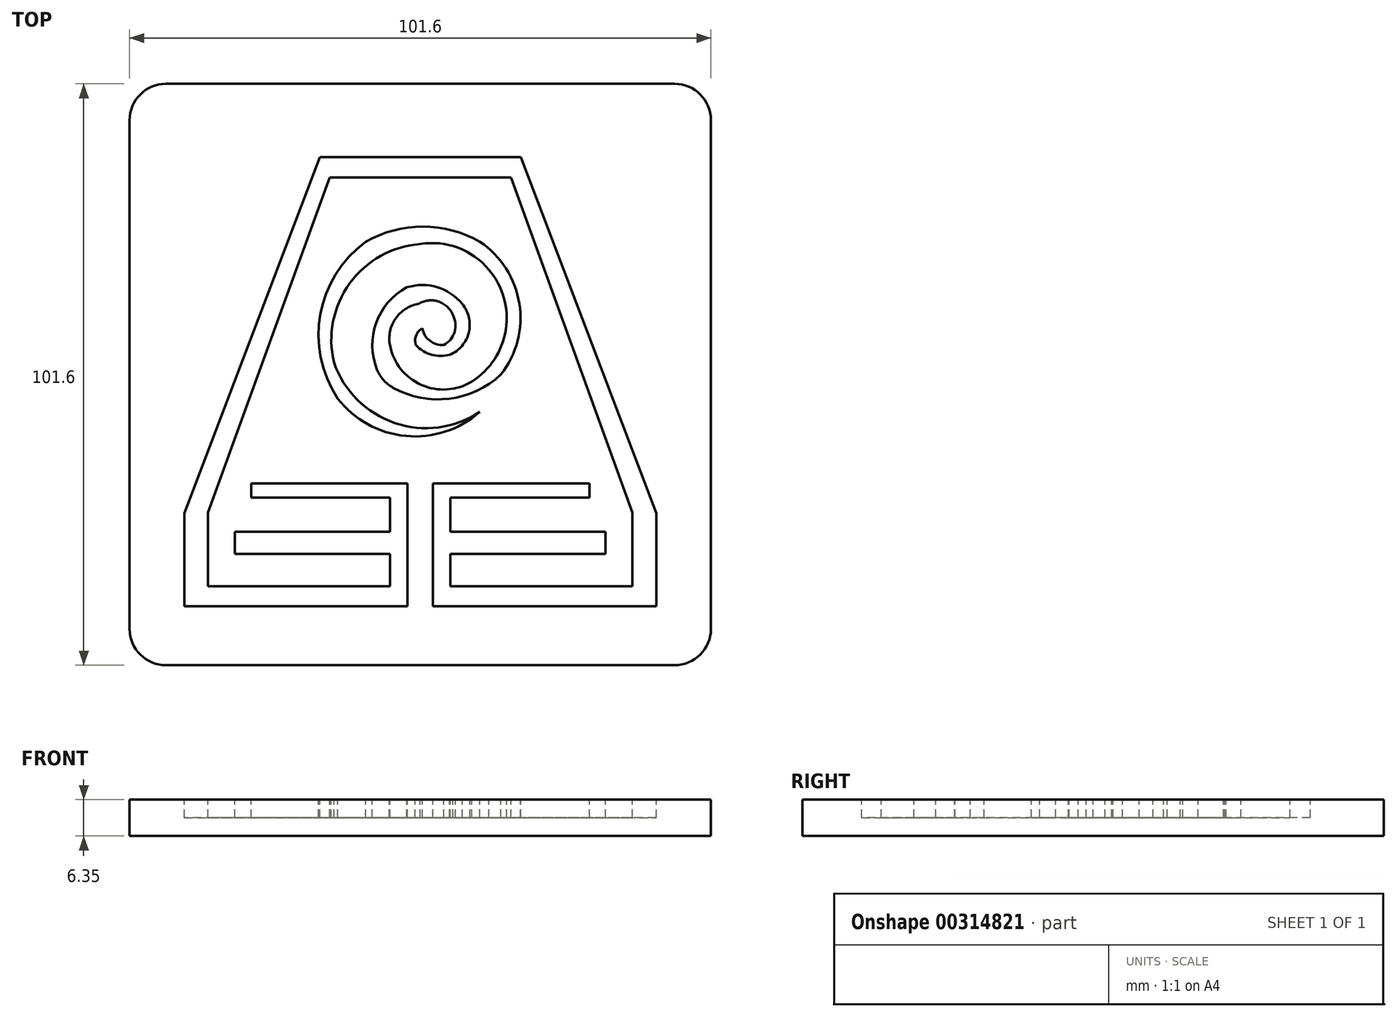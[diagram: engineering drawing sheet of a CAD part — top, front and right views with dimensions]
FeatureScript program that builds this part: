
annotation { "Feature Type Name" : "Feature", "Feature Type Description" : "" }
export const myFeature = defineFeature(function(context is Context, id is Id, definition is map)
    precondition{}
    {
        {
            var Q0;
            Q0=qCreatedBy(makeId("Top.planeOp"),FACE);
            var sketch = newSketch(context, id + "F0", { "sketchPlane" : qUnion([Q0])});
            skLineSegment(sketch, "E0.bottom", {"start": v(-44.45, 50.8) * mm, "end": v(44.45, 50.8) * mm});
            skLineSegment(sketch, "E0.top", {"start": v(-44.45, -50.8) * mm, "end": v(44.45, -50.8) * mm});
            skLineSegment(sketch, "E0.left", {"start": v(-50.8, 44.45) * mm, "end": v(-50.8, -44.45) * mm});
            skLineSegment(sketch, "E0.right", {"start": v(50.8, 44.45) * mm, "end": v(50.8, -44.45) * mm});
            skPoint(sketch, "E1.visualSharp", {"position": v(-50.8, 50.8) * mm});
            skArc(sketch, "E1.filletArc", {"start": v(-44.45, 50.8) * mm, "mid": v(-48.94, 48.94) * mm, "end": v(-50.8, 44.45) * mm});
            skPoint(sketch, "E2.visualSharp", {"position": v(50.8, 50.8) * mm});
            skArc(sketch, "E2.filletArc", {"start": v(50.8, 44.45) * mm, "mid": v(48.94, 48.94) * mm, "end": v(44.45, 50.8) * mm});
            skPoint(sketch, "E3.visualSharp", {"position": v(50.8, -50.8) * mm});
            skArc(sketch, "E3.filletArc", {"start": v(44.45, -50.8) * mm, "mid": v(48.94, -48.94) * mm, "end": v(50.8, -44.45) * mm});
            skPoint(sketch, "E4.visualSharp", {"position": v(-50.8, -50.8) * mm});
            skArc(sketch, "E4.filletArc", {"start": v(-50.8, -44.45) * mm, "mid": v(-48.94, -48.94) * mm, "end": v(-44.45, -50.8) * mm});
            skSolve(sketch);
        }
        {
            var Q0;
            Q0 = qSketchRegion(id + "F0", true);
            extrude(context, id + "F1", {"entities" : qUnion([Q0]), "depth" : 6.35 * mm});
        }
        {
            var Q0;
            Q0=makeQuery(id+"F1.opExtrude","CAP_FACE",FACE,{"disambiguationData":[OSD([sQuery(id+"F0.wireOp",EDGE,"E0.bottom"),sQuery(id+"F0.wireOp",EDGE,"E0.top"),sQuery(id+"F0.wireOp",EDGE,"E0.left"),sQuery(id+"F0.wireOp",EDGE,"E0.right"),sQuery(id+"F0.wireOp",EDGE,"E1.filletArc"),sQuery(id+"F0.wireOp",EDGE,"E2.filletArc"),sQuery(id+"F0.wireOp",EDGE,"E3.filletArc"),sQuery(id+"F0.wireOp",EDGE,"E4.filletArc")])],"isStart":false});
            var sketch = newSketch(context, id + "F2", { "sketchPlane" : qUnion([Q0])});
            skLineSegment(sketch, "E5", {"start": v(-29.55, -19.05) * mm, "end": v(-29.55, -21.48) * mm});
            skLineSegment(sketch, "E6", {"start": v(-29.55, -21.48) * mm, "end": v(-5.27, -21.48) * mm});
            skLineSegment(sketch, "E7", {"start": v(-5.27, -21.48) * mm, "end": v(-5.27, -27.48) * mm});
            skLineSegment(sketch, "E8", {"start": v(-5.27, -27.48) * mm, "end": v(-32.4, -27.48) * mm});
            skLineSegment(sketch, "E9", {"start": v(-32.4, -27.48) * mm, "end": v(-32.4, -31.34) * mm});
            skLineSegment(sketch, "E10", {"start": v(-32.4, -31.34) * mm, "end": v(-5.27, -31.34) * mm});
            skLineSegment(sketch, "E11", {"start": v(-5.27, -31.34) * mm, "end": v(-5.27, -37.03) * mm});
            skLineSegment(sketch, "E12", {"start": v(-5.27, -37.03) * mm, "end": v(-37.07, -37.03) * mm});
            skLineSegment(sketch, "E13", {"start": v(-37.07, -37.03) * mm, "end": v(-37.07, -24.13) * mm});
            skLineSegment(sketch, "E14", {"start": v(-37.07, -24.13) * mm, "end": v(-15.84, 34.42) * mm});
            skLineSegment(sketch, "E15", {"start": v(-15.84, 34.42) * mm, "end": v(0, 34.42) * mm});
            skLineSegment(sketch, "E16", {"start": v(0, 37.97) * mm, "end": v(-17.57, 37.97) * mm});
            skLineSegment(sketch, "E17", {"start": v(-17.57, 37.97) * mm, "end": v(-41.25, -24.24) * mm});
            skLineSegment(sketch, "E18", {"start": v(-41.25, -24.24) * mm, "end": v(-41.25, -40.49) * mm});
            skLineSegment(sketch, "E19", {"start": v(-41.25, -40.49) * mm, "end": v(-2.23, -40.49) * mm});
            skLineSegment(sketch, "E20", {"start": v(-2.23, -40.49) * mm, "end": v(-2.23, -19.05) * mm});
            skLineSegment(sketch, "E21", {"start": v(-2.23, -19.05) * mm, "end": v(-29.55, -19.05) * mm});
            skLineSegment(sketch, "E22", {"start": v(0, 0) * mm, "end": v(0, -12.44) * mm, "construction": true});
            skLineSegment(sketch, "E23.MirrorCS", {"start": v(29.55, -19.05) * mm, "end": v(29.55, -21.48) * mm});
            skLineSegment(sketch, "E24.MirrorCS", {"start": v(5.27, -21.48) * mm, "end": v(5.27, -27.48) * mm});
            skLineSegment(sketch, "E25.MirrorCS", {"start": v(5.27, -27.48) * mm, "end": v(32.4, -27.48) * mm});
            skLineSegment(sketch, "E26.MirrorCS", {"start": v(29.55, -21.48) * mm, "end": v(5.27, -21.48) * mm});
            skLineSegment(sketch, "E27.MirrorCS", {"start": v(32.4, -27.48) * mm, "end": v(32.4, -31.34) * mm});
            skLineSegment(sketch, "E28.MirrorCS", {"start": v(32.4, -31.34) * mm, "end": v(5.27, -31.34) * mm});
            skLineSegment(sketch, "E29.MirrorCS", {"start": v(5.27, -31.34) * mm, "end": v(5.27, -37.03) * mm});
            skLineSegment(sketch, "E30.MirrorCS", {"start": v(5.27, -37.03) * mm, "end": v(37.07, -37.03) * mm});
            skLineSegment(sketch, "E31.MirrorCS", {"start": v(37.07, -37.03) * mm, "end": v(37.07, -24.13) * mm});
            skLineSegment(sketch, "E32.MirrorCS", {"start": v(2.23, -19.05) * mm, "end": v(29.55, -19.05) * mm});
            skLineSegment(sketch, "E33.MirrorCS", {"start": v(41.25, -40.49) * mm, "end": v(2.23, -40.49) * mm});
            skLineSegment(sketch, "E34.MirrorCS", {"start": v(2.23, -40.49) * mm, "end": v(2.23, -19.05) * mm});
            skLineSegment(sketch, "E35.MirrorCS", {"start": v(37.07, -24.13) * mm, "end": v(15.84, 34.42) * mm});
            skLineSegment(sketch, "E36.MirrorCS", {"start": v(17.57, 37.97) * mm, "end": v(41.25, -24.24) * mm});
            skLineSegment(sketch, "E37.MirrorCS", {"start": v(0, 37.97) * mm, "end": v(17.57, 37.97) * mm});
            skLineSegment(sketch, "E38.MirrorCS", {"start": v(15.84, 34.42) * mm, "end": v(0, 34.42) * mm});
            skLineSegment(sketch, "E39.MirrorCS", {"start": v(41.25, -24.24) * mm, "end": v(41.25, -40.49) * mm});
            skArc(sketch, "E40", {"start": v(-14.43, -4.2) * mm, "mid": v(-2.52, -10.74) * mm, "end": v(10.4, -6.54) * mm});
            skArc(sketch, "E41", {"start": v(-15.08, 2.08) * mm, "mid": v(-4.45, -8.47) * mm, "end": v(10.4, -6.54) * mm});
            skArc(sketch, "E42", {"start": v(-9.52, 23.21) * mm, "mid": v(-17.46, 10.49) * mm, "end": v(-14.43, -4.2) * mm});
            skArc(sketch, "E43", {"start": v(0, 22.8) * mm, "mid": v(-12.33, 15.93) * mm, "end": v(-15.08, 2.08) * mm});
            skArc(sketch, "E44", {"start": v(10.4, 23.21) * mm, "mid": v(0.44, 25.85) * mm, "end": v(-9.52, 23.21) * mm});
            skArc(sketch, "E45", {"start": v(14.11, 0) * mm, "mid": v(17.31, 12.41) * mm, "end": v(10.4, 23.21) * mm});
            skArc(sketch, "E46", {"start": v(-4.76, -2.3) * mm, "mid": v(5.05, -4.22) * mm, "end": v(14.11, 0) * mm});
            skArc(sketch, "E47", {"start": v(-2.34, 15.23) * mm, "mid": v(-7.71, 9.04) * mm, "end": v(-7.56, 0.85) * mm});
            skArc(sketch, "E48", {"start": v(7.34, 12.33) * mm, "mid": v(2.94, 15.26) * mm, "end": v(-2.34, 15.23) * mm});
            skArc(sketch, "E49", {"start": v(5.16, 3.46) * mm, "mid": v(8.49, 7.34) * mm, "end": v(7.34, 12.33) * mm});
            skArc(sketch, "E50", {"start": v(-0.72, 5.1) * mm, "mid": v(2, 3.47) * mm, "end": v(5.16, 3.46) * mm});
            skArc(sketch, "E51", {"start": v(0.36, 8.06) * mm, "mid": v(-0.73, 6.83) * mm, "end": v(-0.77, 5.18) * mm});
            skArc(sketch, "E52", {"start": v(0.36, 8.06) * mm, "mid": v(1.69, 5.9) * mm, "end": v(4.12, 5.14) * mm});
            skArc(sketch, "E53", {"start": v(4.12, 5.14) * mm, "mid": v(5.99, 7.48) * mm, "end": v(5.67, 10.45) * mm});
            skArc(sketch, "E54", {"start": v(5.67, 10.45) * mm, "mid": v(3.12, 12.78) * mm, "end": v(-0.3, 12.35) * mm});
            skArc(sketch, "E55", {"start": v(-0.38, 12.32) * mm, "mid": v(-4.34, 9.76) * mm, "end": v(-5.3, 5.14) * mm});
            skArc(sketch, "E56", {"start": v(-5.3, 5.14) * mm, "mid": v(0.19, -1.81) * mm, "end": v(9.02, -1.22) * mm});
            skArc(sketch, "E57", {"start": v(9.02, -1.22) * mm, "mid": v(14.96, 7.86) * mm, "end": v(12, 18.3) * mm});
            skArc(sketch, "E58", {"start": v(12, 18.3) * mm, "mid": v(6.6, 22.16) * mm, "end": v(0, 22.8) * mm});
            skPoint(sketch, "E59.visualSharp", {"position": v(-6.45, -1.22) * mm});
            skArc(sketch, "E59.filletArc", {"start": v(-7.56, 0.85) * mm, "mid": v(-6.43, -0.96) * mm, "end": v(-4.76, -2.3) * mm});
            skPoint(sketch, "E60.visualSharp", {"position": v(-0.75, 5.14) * mm});
            skArc(sketch, "E60.filletArc", {"start": v(-0.77, 5.18) * mm, "mid": v(-0.75, 5.14) * mm, "end": v(-0.72, 5.1) * mm});
            skPoint(sketch, "E61.visualSharp", {"position": v(-0.34, 12.33) * mm});
            skArc(sketch, "E61.filletArc", {"start": v(-0.38, 12.32) * mm, "mid": v(-0.34, 12.33) * mm, "end": v(-0.3, 12.35) * mm});
            skSolve(sketch);
        }
        {
            var Q0;
            Q0 = qSketchRegion(id + "F2", true);
            extrude(context, id + "F3", {"entities" : qUnion([Q0]), "operationType" : NewBodyOperationType.REMOVE, "oppositeDirection" : true, "depth" : 3.17 * mm});
        }
    });
